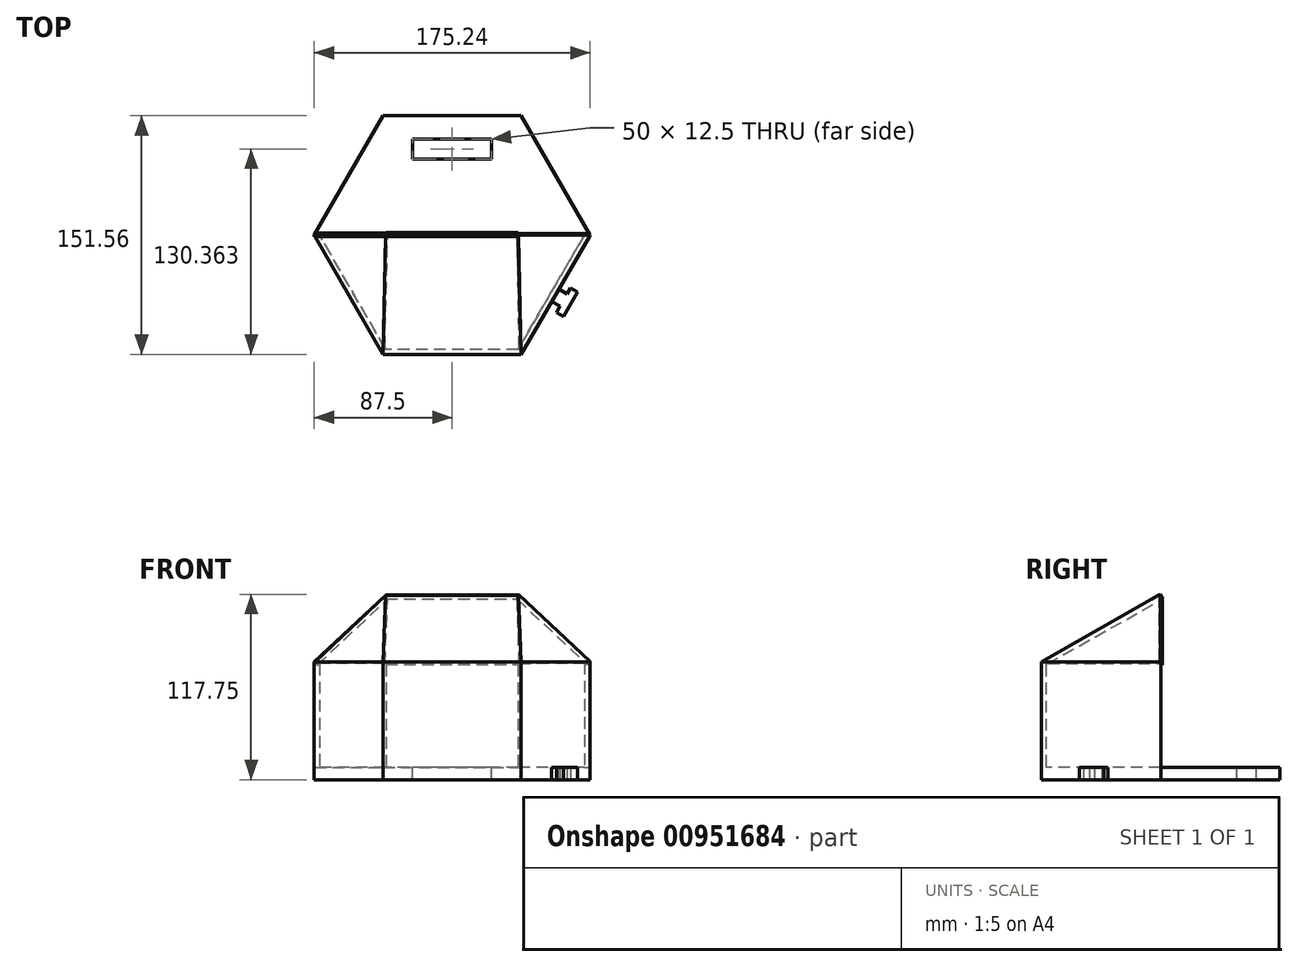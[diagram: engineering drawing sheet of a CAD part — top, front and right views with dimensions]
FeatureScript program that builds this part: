
annotation { "Feature Type Name" : "Feature", "Feature Type Description" : "" }
export const myFeature = defineFeature(function(context is Context, id is Id, definition is map)
    precondition{}
    {
        {
            var Q0;
            Q0=qCreatedBy(makeId("Top.planeOp"),FACE);
            var sketch = newSketch(context, id + "F0", { "sketchPlane" : qUnion([Q0])});
            skCircle(sketch, "E0.cCircle", {"center": v(0, 0) * mm, "radius": 75.78 * mm, "construction": true});
            skLineSegment(sketch, "E0.0", {"start": v(-43.75, 75.78) * mm, "end": v(43.75, 75.78) * mm});
            skLineSegment(sketch, "E0.1", {"start": v(43.75, 75.78) * mm, "end": v(87.5, 0) * mm});
            skLineSegment(sketch, "E0.2", {"start": v(87.5, 0) * mm, "end": v(43.75, -75.78) * mm});
            skLineSegment(sketch, "E0.3", {"start": v(43.75, -75.78) * mm, "end": v(-43.75, -75.78) * mm});
            skLineSegment(sketch, "E0.4", {"start": v(-43.75, -75.78) * mm, "end": v(-87.5, 0) * mm});
            skLineSegment(sketch, "E0.5", {"start": v(-87.5, 0) * mm, "end": v(-43.75, 75.78) * mm});
            skPoint(sketch, "E0.0.midPoint", {"position": v(0, 75.78) * mm});
            skLineSegment(sketch, "E1.0", {"start": v(-84.04, 0) * mm, "end": v(-42.02, 72.78) * mm});
            skLineSegment(sketch, "E1.1", {"start": v(42.02, 72.78) * mm, "end": v(84.04, 0) * mm});
            skLineSegment(sketch, "E1.2", {"start": v(84.04, 0) * mm, "end": v(42.02, -72.78) * mm});
            skLineSegment(sketch, "E1.3", {"start": v(-42.02, 72.78) * mm, "end": v(42.02, 72.78) * mm});
            skLineSegment(sketch, "E1.4", {"start": v(42.02, -72.78) * mm, "end": v(-42.02, -72.78) * mm});
            skLineSegment(sketch, "E1.5", {"start": v(-42.02, -72.78) * mm, "end": v(-84.04, 0) * mm});
            skLineSegment(sketch, "E2", {"start": v(-87.5, 0) * mm, "end": v(-84.04, 0) * mm});
            skLineSegment(sketch, "E3", {"start": v(84.04, 0) * mm, "end": v(87.5, 0) * mm});
            skLineSegment(sketch, "E4", {"start": v(0, 0) * mm, "end": v(0, 72.78) * mm, "construction": true});
            skLineSegment(sketch, "E5", {"start": v(0, 0) * mm, "end": v(42.02, 72.78) * mm, "construction": true});
            skLineSegment(sketch, "E6", {"start": v(0, 0) * mm, "end": v(-42.02, 72.78) * mm, "construction": true});
            skLineSegment(sketch, "E7", {"start": v(0, 36.39) * mm, "end": v(0, 72.78) * mm, "construction": true});
            skLineSegment(sketch, "E8.bottom", {"start": v(25, 48.33) * mm, "end": v(-25, 48.33) * mm});
            skLineSegment(sketch, "E8.top", {"start": v(25, 60.83) * mm, "end": v(-25, 60.83) * mm});
            skLineSegment(sketch, "E8.left", {"start": v(25, 48.33) * mm, "end": v(25, 60.83) * mm});
            skLineSegment(sketch, "E8.right", {"start": v(-25, 48.33) * mm, "end": v(-25, 60.83) * mm});
            skPoint(sketch, "E8.middle", {"position": v(0, 54.58) * mm});
            skLineSegment(sketch, "E9", {"start": v(-65.63, 37.89) * mm, "end": v(-68.13, 33.56) * mm});
            skLineSegment(sketch, "E10.MirrorCS", {"start": v(87.5, 0) * mm, "end": v(43.75, 75.78) * mm});
            skPoint(sketch, "E11.endSnap0", {"position": v(-68.4, -45.1) * mm});
            skLineSegment(sketch, "E12.MirrorCS", {"start": v(66.4, -49.14) * mm, "end": v(70.72, -51.67) * mm});
            skLineSegment(sketch, "E13.MirrorCS", {"start": v(72.98, -47.75) * mm, "end": v(70.72, -51.67) * mm});
            skLineSegment(sketch, "E14.MirrorCS", {"start": v(72.98, -47.75) * mm, "end": v(63.2, -42.1) * mm});
            skLineSegment(sketch, "E15.MirrorCS", {"start": v(77.48, -39.96) * mm, "end": v(72.98, -47.75) * mm});
            skLineSegment(sketch, "E16.MirrorCS", {"start": v(77.48, -39.96) * mm, "end": v(67.7, -34.3) * mm});
            skLineSegment(sketch, "E17.MirrorCS", {"start": v(75.4, -33.57) * mm, "end": v(79.7, -36.12) * mm});
            skLineSegment(sketch, "E18.MirrorCS", {"start": v(77.48, -39.96) * mm, "end": v(79.7, -36.12) * mm});
            skLineSegment(sketch, "E19", {"start": v(75.4, -33.57) * mm, "end": v(73.15, -37.46) * mm});
            skLineSegment(sketch, "E20", {"start": v(66.4, -49.14) * mm, "end": v(68.65, -45.25) * mm});
            skSolve(sketch);
        }
        {
            var Q0;
            Q0=makeQuery(id+"F0.imprint","IMPRINT",FACE,{"disambiguationData":[TD([[makeQuery(id+"F0.imprint","IMPRINT",EDGE,{"derivedFrom":sQuery(id+"F0.wireOp",EDGE,"E1.0")}),-1.0]])]});
            extrude(context, id + "F1", {"entities" : qUnion([Q0]), "depth" : 8 * mm, "offsetDistance" : 25 * mm});
        }
        {
            var Q0;
            Q0=makeQuery(id+"F0.imprint","IMPRINT",FACE,{"disambiguationData":[TD([[makeQuery(id+"F0.imprint","IMPRINT",EDGE,{"derivedFrom":sQuery(id+"F0.wireOp",EDGE,"E0.2")}),-1.0]])]});
            extrude(context, id + "F2", {"entities" : qUnion([Q0]), "operationType" : NewBodyOperationType.ADD, "depth" : 75 * mm, "offsetDistance" : 25 * mm});
        }
        {
            var Q0;
            Q0=qCreatedBy(makeId("Front.planeOp"),FACE);
            var sketch = newSketch(context, id + "F3", { "sketchPlane" : qUnion([Q0])});
            skLineSegment(sketch, "E21", {"start": v(0, 0) * mm, "end": v(0, 144.27) * mm, "construction": true});
            skLineSegment(sketch, "E22", {"start": v(0, 144.27) * mm, "end": v(-94, 144.27) * mm, "construction": true});
            skLineSegment(sketch, "E23", {"start": v(0, 144.27) * mm, "end": v(81.74, 144.27) * mm});
            skLineSegment(sketch, "E24", {"start": v(0, 0) * mm, "end": v(0, 75) * mm, "construction": true});
            skLineSegment(sketch, "E25", {"start": v(0, 75) * mm, "end": v(0, 114.5) * mm, "construction": true});
            skLineSegment(sketch, "E26", {"start": v(0, 75) * mm, "end": v(-87.5, 75) * mm, "construction": true});
            skLineSegment(sketch, "E27", {"start": v(0, 114.5) * mm, "end": v(42.02, 114.5) * mm, "construction": true});
            skLineSegment(sketch, "E28", {"start": v(0, 114.5) * mm, "end": v(-42.02, 114.5) * mm});
            skLineSegment(sketch, "E29", {"start": v(0, 75) * mm, "end": v(-84.04, 75) * mm, "construction": true});
            skLineSegment(sketch, "E30", {"start": v(-42.02, 114.5) * mm, "end": v(-84.04, 75) * mm});
            skLineSegment(sketch, "E31", {"start": v(-42.02, 114.5) * mm, "end": v(-42.02, 117.5) * mm, "construction": true});
            skLineSegment(sketch, "E32", {"start": v(-42.02, 117.5) * mm, "end": v(-87.5, 75) * mm});
            skLineSegment(sketch, "E33", {"start": v(-42.02, 117.5) * mm, "end": v(0, 117.5) * mm});
            skLineSegment(sketch, "E34.MirrorCS", {"start": v(42.02, 117.5) * mm, "end": v(87.5, 75) * mm});
            skLineSegment(sketch, "E35.MirrorCS", {"start": v(42.02, 114.5) * mm, "end": v(84.04, 75) * mm});
            skLineSegment(sketch, "E36.MirrorCS", {"start": v(42.02, 117.5) * mm, "end": v(0, 117.5) * mm});
            skLineSegment(sketch, "E37.MirrorCS", {"start": v(0, 114.5) * mm, "end": v(42.02, 114.5) * mm});
            skLineSegment(sketch, "E38", {"start": v(87.5, 75) * mm, "end": v(84.04, 75) * mm});
            skLineSegment(sketch, "E39", {"start": v(-84.04, 75) * mm, "end": v(-87.5, 75) * mm});
            skSolve(sketch);
        }
        {
            var Q0;
            Q0=makeQuery(id+"F0.imprint","IMPRINT",FACE,{"disambiguationData":[TD([[makeQuery(id+"F0.imprint","IMPRINT",EDGE,{"derivedFrom":sQuery(id+"F0.wireOp",EDGE,"E0.0")}),-1.0]])]});
            extrude(context, id + "F4", {"entities" : qUnion([Q0]), "operationType" : NewBodyOperationType.ADD, "oppositeDirection" : true, "depth" : -8 * mm, "offsetDistance" : 25 * mm});
        }
        {
            var Q0;
            Q0=makeQuery(id+"F2.opExtrude","CAP_EDGE",EDGE,{"disambiguationData":[OSD([sQuery(id+"F0.wireOp",EDGE,"E0.3")])],"isStart":false});
            var Q1;
            Q1=sQuery(id+"F3.wireOp",VERTEX,"E33.end");
            cPlane(context, id + "F5", {"entities" : qUnion([Q0, Q1]), "cplaneType" : CPlaneType.LINE_ANGLE, "offset" : 25 * mm, "angle" : 0 * degree, "width" : 150 * mm, "height" : 150 * mm});
        }
        {
            var Q0;
            Q0=qCreatedBy(id+"F5.planeOp",FACE);
            var sketch = newSketch(context, id + "F6", { "sketchPlane" : qUnion([Q0])});
            skLineSegment(sketch, "E40", {"start": v(0, 29.4) * mm, "end": v(43.75, 29.4) * mm});
            skLineSegment(sketch, "E41", {"start": v(0, 29.4) * mm, "end": v(-43.75, 29.4) * mm});
            skLineSegment(sketch, "E42", {"start": v(-43.75, 29.4) * mm, "end": v(-42.02, -57.48) * mm});
            skLineSegment(sketch, "E43", {"start": v(43.75, 29.4) * mm, "end": v(42.02, -57.48) * mm});
            skLineSegment(sketch, "E44", {"start": v(-42.02, -57.48) * mm, "end": v(42.02, -57.48) * mm});
            skSolve(sketch);
        }
        {
            var Q0;
            Q0=makeQuery(id+"F6.imprint","IMPRINT",FACE,{"disambiguationData":[TD([[makeQuery(id+"F6.imprint","IMPRINT",EDGE,{"derivedFrom":sQuery(id+"F6.wireOp",EDGE,"E40")}),-1.0]])]});
            extrude(context, id + "F7", {"entities" : qUnion([Q0]), "operationType" : NewBodyOperationType.ADD, "depth" : 3 * mm, "offsetDistance" : 25 * mm});
        }
        {
            var Q0;
            Q0=makeQuery(id+"F3.imprint","IMPRINT",FACE,{"disambiguationData":[TD([[makeQuery(id+"F3.imprint","IMPRINT",EDGE,{"derivedFrom":sQuery(id+"F3.wireOp",EDGE,"E28")}),-1.0]])]});
            extrude(context, id + "F8", {"entities" : qUnion([Q0]), "operationType" : NewBodyOperationType.ADD, "depth" : 1 * mm, "offsetDistance" : 25 * mm});
        }
        {
            var Q0;
            Q0=makeQuery(id+"F8.opExtrude","CAP_EDGE",EDGE,{"disambiguationData":[OSD([sQuery(id+"F3.wireOp",EDGE,"E32")])],"isStart":true});
            var Q1;
            Q1=makeQuery(id+"F7.boolean.opBoolean","MERGE",VERTEX,{"derivedFrom":[makeQuery(id+"F2.opExtrude","CAP_VERTEX",VERTEX,{"disambiguationData":[OSD([sQuery(id+"F0.wireOp",EDGE,"E0.3"),sQuery(id+"F0.wireOp",EDGE,"E0.4")])],"isStart":false}),makeQuery(id+"F7.opExtrude","CAP_VERTEX",VERTEX,{"disambiguationData":[OSD([sQuery(id+"F6.wireOp",EDGE,"E41"),sQuery(id+"F6.wireOp",EDGE,"E42")])],"isStart":true})]});
            cPlane(context, id + "F9", {"entities" : qUnion([Q0, Q1]), "cplaneType" : CPlaneType.LINE_ANGLE, "offset" : 25 * mm, "angle" : 0 * degree, "width" : 150 * mm, "height" : 150 * mm});
        }
        {
            var Q0;
            Q0=qCreatedBy(id+"F9.planeOp",FACE);
            var sketch = newSketch(context, id + "F10", { "sketchPlane" : qUnion([Q0])});
            skLineSegment(sketch, "E45", {"start": v(-25.66, 35.61) * mm, "end": v(30.99, -31.08) * mm});
            skLineSegment(sketch, "E46", {"start": v(-25.66, 35.61) * mm, "end": v(33.23, 55.79) * mm});
            skLineSegment(sketch, "E47", {"start": v(33.23, 55.79) * mm, "end": v(30.99, -31.08) * mm});
            skSolve(sketch);
        }
        {
            var Q0;
            Q0=qSketchRegion(id+"F10",true);
            extrude(context, id + "F11", {"entities" : qUnion([Q0]), "operationType" : NewBodyOperationType.ADD, "depth" : -3 * mm, "offsetDistance" : 25 * mm});
        }
        {
            var Q0;
            Q0=makeQuery(id+"F8.opExtrude","CAP_EDGE",EDGE,{"disambiguationData":[OSD([sQuery(id+"F3.wireOp",EDGE,"E34.MirrorCS")])],"isStart":false});
            var Q1;
            Q1=makeQuery(id+"F7.boolean.opBoolean","MERGE",VERTEX,{"derivedFrom":[makeQuery(id+"F2.opExtrude","CAP_VERTEX",VERTEX,{"disambiguationData":[OSD([sQuery(id+"F0.wireOp",EDGE,"E0.2"),sQuery(id+"F0.wireOp",EDGE,"E0.3")])],"isStart":false}),makeQuery(id+"F7.opExtrude","CAP_VERTEX",VERTEX,{"disambiguationData":[OSD([sQuery(id+"F6.wireOp",EDGE,"E40"),sQuery(id+"F6.wireOp",EDGE,"E43")])],"isStart":true})]});
            cPlane(context, id + "F12", {"entities" : qUnion([Q0, Q1]), "cplaneType" : CPlaneType.LINE_ANGLE, "offset" : 25 * mm, "angle" : 0 * degree, "width" : 150 * mm, "height" : 150 * mm});
        }
        {
            var Q0;
            Q0=qCreatedBy(id+"F12.planeOp",FACE);
            var sketch = newSketch(context, id + "F13", { "sketchPlane" : qUnion([Q0])});
            skLineSegment(sketch, "E48", {"start": v(-32.88, -56.36) * mm, "end": v(25.94, -35.98) * mm});
            skLineSegment(sketch, "E49", {"start": v(25.94, -35.98) * mm, "end": v(-30.94, 30.51) * mm});
            skLineSegment(sketch, "E50", {"start": v(-30.94, 30.51) * mm, "end": v(-32.88, -56.36) * mm});
            skSolve(sketch);
        }
        {
            var Q0;
            Q0=qSketchRegion(id+"F13",true);
            extrude(context, id + "F14", {"entities" : qUnion([Q0]), "operationType" : NewBodyOperationType.ADD, "depth" : 3 * mm, "offsetDistance" : 25 * mm});
        }
        {
            var Q0;
            Q0=makeQuery(id+"F0.imprint","IMPRINT",FACE,{"disambiguationData":[TD([[makeQuery(id+"F0.imprint","IMPRINT",EDGE,{"derivedFrom":sQuery(id+"F0.wireOp",EDGE,"E8.bottom")}),-1.0]])]});
            extrude(context, id + "F15", {"entities" : qUnion([Q0]), "operationType" : NewBodyOperationType.ADD, "depth" : 8 * mm, "offsetDistance" : 25 * mm});
        }
        {
            var Q0;
            {var subQ5=sQuery(id+"F0.wireOp",EDGE,"749d55a2-1ae5-4b90-8efe-ab6072e4ac770.MirrorCS");Q0=makeQuery(id+"F0.imprint","IMPRINT",FACE,{"disambiguationData":[TD([[makeQuery(id+"F0.imprint","IMPRINT",EDGE,{"derivedFrom":subQ5}),1.0]])]});}
            var Q1;
            {var subQ4=sQuery(id+"F0.wireOp",EDGE,"bf9a6782-c77d-4324-b6f4-6efb0bd9360c0.MirrorCS");Q1=makeQuery(id+"F0.imprint","IMPRINT",FACE,{"disambiguationData":[TD([[makeQuery(id+"F0.imprint","IMPRINT",EDGE,{"derivedFrom":subQ4}),1.0]])]});}
            var Q2;
            {var subQ0=sQuery(id+"F0.wireOp",EDGE,"c1ebaf2c-39ee-4834-980c-edcd090fc9720.MirrorCS");Q2=makeQuery(id+"F0.imprint","IMPRINT",FACE,{"disambiguationData":[TD([[makeQuery(id+"F0.imprint","IMPRINT",EDGE,{"derivedFrom":subQ0}),1.0]])]});}
            var Q3;
            {var subQ5=sQuery(id+"F0.wireOp",EDGE,"E17.MirrorCS");Q3=makeQuery(id+"F0.imprint","IMPRINT",FACE,{"disambiguationData":[TD([[makeQuery(id+"F0.imprint","IMPRINT",EDGE,{"derivedFrom":subQ5}),-1.0]])]});}
            var Q4;
            {var subQ0=sQuery(id+"F0.wireOp",EDGE,"E15.MirrorCS");Q4=makeQuery(id+"F0.imprint","IMPRINT",FACE,{"disambiguationData":[TD([[makeQuery(id+"F0.imprint","IMPRINT",EDGE,{"derivedFrom":subQ0}),-1.0]])]});}
            var Q5;
            {var subQ0=sQuery(id+"F0.wireOp",EDGE,"bff1d7ab-137b-4689-a84f-e4ae87ef17b20.MirrorCS");Q5=makeQuery(id+"F0.imprint","IMPRINT",FACE,{"disambiguationData":[TD([[makeQuery(id+"F0.imprint","IMPRINT",EDGE,{"derivedFrom":subQ0}),1.0]])]});}
            extrude(context, id + "F16", {"entities" : qUnion([Q0, Q1, Q2, Q3, Q4, Q5]), "operationType" : NewBodyOperationType.ADD, "depth" : 8 * mm, "offsetDistance" : 25 * mm});
        }
        {
            var Q0;
            Q0=makeQuery(id+"F0.imprint","IMPRINT",FACE,{"disambiguationData":[TD([[makeQuery(id+"F0.imprint","IMPRINT",EDGE,{"derivedFrom":sQuery(id+"F0.wireOp",EDGE,"E8.bottom")}),-1.0]])]});
            extrude(context, id + "F17", {"entities" : qUnion([Q0]), "operationType" : NewBodyOperationType.REMOVE, "endBound" : BoundingType.SYMMETRIC, "oppositeDirection" : true, "depth" : 25 * mm, "offsetDistance" : 25 * mm});
        }
        {
            var Q0;
            Q0=makeQuery(id+"F0.imprint","IMPRINT",FACE,{"disambiguationData":[TD([[makeQuery(id+"F0.imprint","IMPRINT",EDGE,{"derivedFrom":sQuery(id+"F0.wireOp",EDGE,"E12.MirrorCS")}),1.0]])]});
            extrude(context, id + "F18", {"entities" : qUnion([Q0]), "operationType" : NewBodyOperationType.ADD, "depth" : 8 * mm, "offsetDistance" : 25 * mm});
        }
    });
